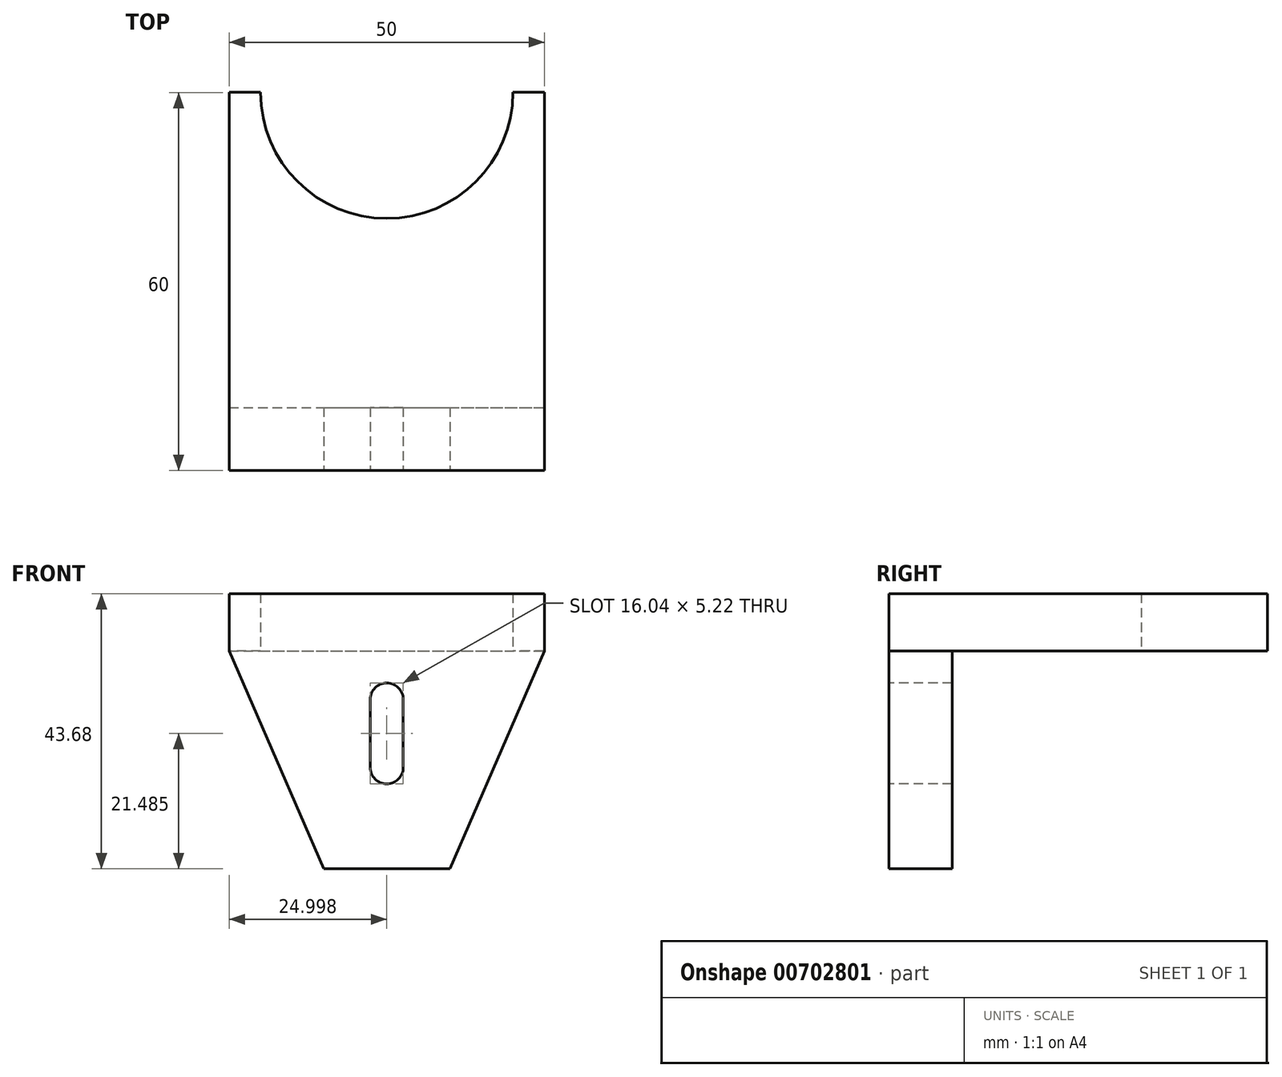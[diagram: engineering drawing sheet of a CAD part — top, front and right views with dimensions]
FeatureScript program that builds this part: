
annotation { "Feature Type Name" : "Feature", "Feature Type Description" : "" }
export const myFeature = defineFeature(function(context is Context, id is Id, definition is map)
    precondition{}
    {
        {
            var Q0;
            Q0=qCreatedBy(makeId("Top.planeOp"),FACE);
            var sketch = newSketch(context, id + "F0", { "sketchPlane" : qUnion([Q0])});
            skLineSegment(sketch, "E0", {"start": v(-50.51, 26.3) * mm, "end": v(-50.51, -33.7) * mm});
            skLineSegment(sketch, "E1", {"start": v(-50.51, -33.7) * mm, "end": v(-0.51, -33.7) * mm});
            skLineSegment(sketch, "E2", {"start": v(-0.51, -33.7) * mm, "end": v(-0.51, 26.3) * mm});
            skLineSegment(sketch, "E3", {"start": v(-0.51, 26.3) * mm, "end": v(-5.51, 26.3) * mm});
            skArc(sketch, "E4", {"start": v(-45.51, 26.3) * mm, "mid": v(-25.51, 6.3) * mm, "end": v(-5.51, 26.3) * mm});
            skLineSegment(sketch, "E5.trimOffspring", {"start": v(-45.51, 26.3) * mm, "end": v(-50.51, 26.3) * mm});
            skSolve(sketch);
        }
        {
            var Q0;
            Q0 = qSketchRegion(id + "F0", true);
            extrude(context, id + "F1", {"entities" : qUnion([Q0]), "depth" : 9.1 * mm, "offsetDistance" : 25 * mm});
        }
        {
            var Q0;
            Q0=makeQuery(id+"F1.opExtrude","SWEPT_FACE",FACE,{"disambiguationData":[OSD([sQuery(id+"F0.wireOp",EDGE,"E1")])]});
            var sketch = newSketch(context, id + "F2", { "sketchPlane" : qUnion([Q0])});
            skLineSegment(sketch, "E6", {"start": v(-50.51, 0) * mm, "end": v(-35.51, -34.58) * mm});
            skLineSegment(sketch, "E7", {"start": v(-35.51, -34.58) * mm, "end": v(-15.51, -34.58) * mm});
            skLineSegment(sketch, "E8", {"start": v(-15.51, -34.58) * mm, "end": v(-0.51, 0) * mm});
            skLineSegment(sketch, "E9", {"start": v(-0.51, 0) * mm, "end": v(-50.51, 0) * mm});
            skArc(sketch, "E10", {"start": v(-22.9, -7.69) * mm, "mid": v(-25.51, -5.08) * mm, "end": v(-28.12, -7.69) * mm});
            skPoint(sketch, "E10.centerSnap0", {"position": v(-25.51, 0) * mm});
            skArc(sketch, "E11", {"start": v(-28.12, -18.5) * mm, "mid": v(-25.51, -21.11) * mm, "end": v(-22.9, -18.5) * mm});
            skLineSegment(sketch, "E12", {"start": v(-28.12, -7.69) * mm, "end": v(-28.12, -18.5) * mm});
            skLineSegment(sketch, "E13", {"start": v(-22.9, -7.69) * mm, "end": v(-22.9, -18.5) * mm});
            skSolve(sketch);
        }
        {
            var Q0;
            Q0 = qSketchRegion(id + "F2", true);
            extrude(context, id + "F3", {"entities" : qUnion([Q0]), "operationType" : NewBodyOperationType.ADD, "oppositeDirection" : true, "depth" : 10 * mm, "offsetDistance" : 25 * mm});
        }
    });
